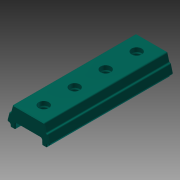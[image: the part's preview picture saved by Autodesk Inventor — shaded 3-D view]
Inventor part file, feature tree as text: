
AUTODESK INVENTOR PART (.ipt)
format: ipt  version: 2011 SP1 (Build 150282100, 282)  size: 1,439,744 bytes
history: native  units: in
note: dims shown in document units (in); Inventor stores cm internally (conversion verified against a paired STEP export)
features: sketch x7, extrude x6, chamfer x5, fillet x4, projected_geometry x2, plane x1, pattern_linear x1, hole x1
ambient origin geometry x8: Origin, YZ Plane, XZ Plane, XY Plane, X Axis, Y Axis, Z Axis, Center Point
bodies: Solid1 (feature_tree)
feature tree (27):
  extrude  "Extrusion1"  Depth=0.011in TaperAngle=45.0deg
  extrude  "Extrusion6"  Depth=0.043in
  extrude  "Extrusion7"  Depth=0.248in
  chamfer  "Chamfer1"  Distance=0.4375in
  extrude  "Extrusion2"  Depth=1.5748in
  plane  "Work Plane2"
  extrude  "Extrusion4"  Depth=1.996in
  pattern_linear  "Rectangular Pattern1"  Spacing1=0.04in  [1 undecoded]
  extrude  "Extrusion5"  Depth=0.1875in TaperAngle=0.0deg
  fillet  "Fillet21"  Radius=0.04in
  fillet  "Fillet23"  Radius=0.054in
  fillet  "Fillet24"  Radius=0.04in
  fillet  "Fillet25"  Radius=0.054in
  hole  "Hole1"  [1 undecoded]
  chamfer  "Chamfer2"  Distance=0.012in
  chamfer  "Chamfer3"  Distance=0.012in
  chamfer  "Chamfer4"  Distance=0.012in
  chamfer  "Chamfer5"  Distance=0.012in
  sketch  "Sketch1"  dims[d0=1.996in d1=0.0in d2=0.011in d3=0.125in d4=45.0deg]
  sketch  "Sketch3"  dims[d6=0.043in d7=0.043in]
  sketch  "Sketch5"  dims[d8=0.175in d9=-0.0069in d18=0.248in]
  sketch  "Sketch8"  dims[d19=0.304in]
  sketch  "Sketch9"  dims[d20=0.04in]
  sketch  "Sketch11"  dims[d21=0.02in]
  sketch  "Sketch12"  dims[d24=0.152in d25=0.4375in d26=0.0in d27=1.5748in d29=0.5in d30=1.996in d32=0.04in d33=0.02in d34=0.1875in d35=0.0in d41=0.04in d42=0.054in d43=0.0in d46=0.04in d47=0.054in d48=0.0in d54=1.5748in d56=0.5in d57=0.3937in d59=1.0in d67=0.012in d69=0.012in d70=0.012in d71=0.012in d72=0.146in d73=0.75in d74=0.165in d75=0.066in d76=0.5635in d77=1.0in d78=0.8108in d79=0.0095in d80=0.125in d81=120.0deg d82=0.0095in d83=0.125in d84=120.0deg d85=0.0095in d86=0.125in d87=120.0deg d88=0.0095in d89=0.125in d90=120.0deg]
  projected_geometry  "Projected Loop2"
  projected_geometry  "Project Cut Edges2"
note: 2 required parameter values undecoded (feature->parameter linkage not recoverable at this tier; creation-order binding heuristic only, values carry confidence <= 0.55)
